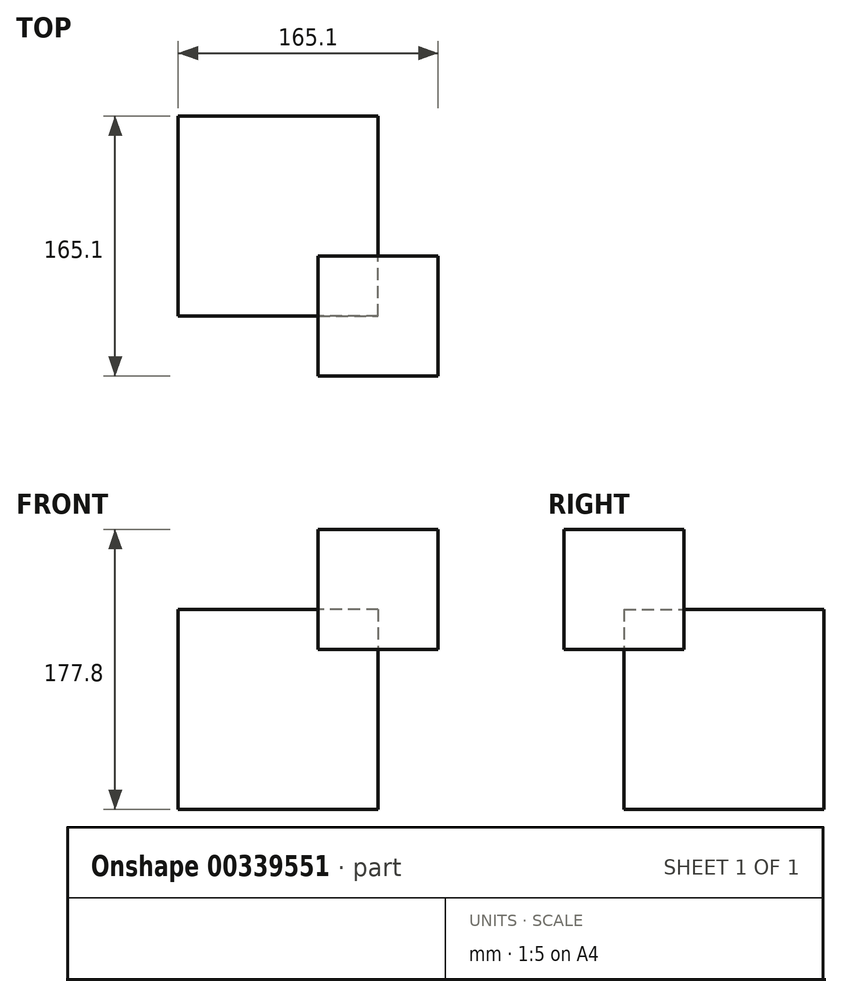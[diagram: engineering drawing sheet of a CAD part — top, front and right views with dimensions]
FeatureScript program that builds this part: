
annotation { "Feature Type Name" : "Feature", "Feature Type Description" : "" }
export const myFeature = defineFeature(function(context is Context, id is Id, definition is map)
    precondition{}
    {
        {
            var Q0;
            Q0=qCreatedBy(makeId("Front.planeOp"),FACE);
            var sketch = newSketch(context, id + "F0", { "sketchPlane" : qUnion([Q0])});
            skLineSegment(sketch, "E0.bottom", {"start": v(63.5, 63.5) * mm, "end": v(-63.5, 63.5) * mm});
            skLineSegment(sketch, "E0.top", {"start": v(63.5, -63.5) * mm, "end": v(-63.5, -63.5) * mm});
            skLineSegment(sketch, "E0.left", {"start": v(63.5, 63.5) * mm, "end": v(63.5, -63.5) * mm});
            skLineSegment(sketch, "E0.right", {"start": v(-63.5, 63.5) * mm, "end": v(-63.5, -63.5) * mm});
            skPoint(sketch, "E0.middle", {"position": v(0, 0) * mm});
            skSolve(sketch);
        }
        {
            var Q0;
            Q0=makeQuery(id+"F0.imprint","IMPRINT",FACE,{"disambiguationData":[TD([[makeQuery(id+"F0.imprint","IMPRINT",EDGE,{"derivedFrom":sQuery(id+"F0.wireOp",EDGE,"E0.bottom")}),1.0]])]});
            extrude(context, id + "F1", {"entities" : qUnion([Q0]), "endBound" : BoundingType.SYMMETRIC, "depth" : 127 * mm});
        }
        {
            var Q0;
            Q0=qCreatedBy(makeId("Top.planeOp"),FACE);
            cPlane(context, id + "F2", {"entities" : qUnion([Q0]), "cplaneType" : CPlaneType.OFFSET, "offset" : 38.1 * mm, "width" : 152.4 * mm, "height" : 152.4 * mm});
        }
        {
            var Q0;
            Q0=qCreatedBy(id+"F2.planeOp",FACE);
            var sketch = newSketch(context, id + "F3", { "sketchPlane" : qUnion([Q0])});
            skLineSegment(sketch, "E1.0.0", {"start": v(63.5, 63.5) * mm, "end": v(-63.5, 63.5) * mm});
            skLineSegment(sketch, "E1.0.1", {"start": v(-63.5, 63.5) * mm, "end": v(-63.5, -63.5) * mm});
            skLineSegment(sketch, "E1.0.2", {"start": v(-63.5, -63.5) * mm, "end": v(63.5, -63.5) * mm});
            skLineSegment(sketch, "E1.0.3", {"start": v(63.5, -63.5) * mm, "end": v(63.5, 63.5) * mm});
            skLineSegment(sketch, "E2.bottom", {"start": v(101.6, -25.4) * mm, "end": v(25.4, -25.4) * mm});
            skLineSegment(sketch, "E2.top", {"start": v(101.6, -101.6) * mm, "end": v(25.4, -101.6) * mm});
            skLineSegment(sketch, "E2.left", {"start": v(101.6, -25.4) * mm, "end": v(101.6, -101.6) * mm});
            skLineSegment(sketch, "E2.right", {"start": v(25.4, -25.4) * mm, "end": v(25.4, -101.6) * mm});
            skPoint(sketch, "E2.middle", {"position": v(63.5, -63.5) * mm});
            skSolve(sketch);
        }
        {
            var Q0;
            {var subQ6=sQuery(id+"F3.wireOp",EDGE,"E2.top");Q0=makeQuery(id+"F3.imprint","IMPRINT",FACE,{"disambiguationData":[TD([[makeQuery(id+"F3.imprint","IMPRINT",EDGE,{"derivedFrom":subQ6}),-1.0]])]});}
            extrude(context, id + "F4", {"entities" : qUnion([Q0]), "operationType" : NewBodyOperationType.ADD, "depth" : 76.2 * mm});
        }
        {
            var Q0;
            Q0=makeQuery(id+"F1.opExtrude","SWEPT_FACE",FACE,{"disambiguationData":[OSD([sQuery(id+"F0.wireOp",EDGE,"E0.bottom")])]});
            var sketch = newSketch(context, id + "F5", { "sketchPlane" : qUnion([Q0])});
            skLineSegment(sketch, "E3.0.0", {"start": v(101.6, -101.6) * mm, "end": v(101.6, -25.4) * mm});
            skLineSegment(sketch, "E3.0.1", {"start": v(101.6, -25.4) * mm, "end": v(63.5, -25.4) * mm});
            skLineSegment(sketch, "E3.0.2", {"start": v(63.5, -25.4) * mm, "end": v(63.5, -63.5) * mm});
            skLineSegment(sketch, "E3.0.3", {"start": v(63.5, -63.5) * mm, "end": v(25.4, -63.5) * mm});
            skLineSegment(sketch, "E3.0.4", {"start": v(25.4, -63.5) * mm, "end": v(25.4, -101.6) * mm});
            skLineSegment(sketch, "E3.0.5", {"start": v(25.4, -101.6) * mm, "end": v(101.6, -101.6) * mm});
            skLineSegment(sketch, "E4.0.0", {"start": v(63.5, 63.5) * mm, "end": v(-63.5, 63.5) * mm});
            skLineSegment(sketch, "E4.0.1", {"start": v(-63.5, 63.5) * mm, "end": v(-63.5, -63.5) * mm});
            skLineSegment(sketch, "E4.0.2", {"start": v(-63.5, -63.5) * mm, "end": v(25.4, -63.5) * mm});
            skLineSegment(sketch, "E4.0.3", {"start": v(25.4, -63.5) * mm, "end": v(63.5, -63.5) * mm});
            skLineSegment(sketch, "E4.0.4", {"start": v(63.5, -63.5) * mm, "end": v(63.5, -25.4) * mm});
            skLineSegment(sketch, "E4.0.5", {"start": v(63.5, -25.4) * mm, "end": v(63.5, 63.5) * mm});
            skLineSegment(sketch, "E5.top", {"start": v(63.5, -25.4) * mm, "end": v(25.4, -25.4) * mm});
            skLineSegment(sketch, "E5.right", {"start": v(25.4, -63.5) * mm, "end": v(25.4, -25.4) * mm});
            skSolve(sketch);
        }
        {
            var Q0;
            Q0=makeQuery(id+"F5.imprint","IMPRINT",FACE,{"disambiguationData":[TD([[makeQuery(id+"F5.imprint","IMPRINT",EDGE,{"derivedFrom":sQuery(id+"F5.wireOp",EDGE,"E3.0.3")}),-1.0]])]});
            extrude(context, id + "F6", {"entities" : qUnion([Q0]), "operationType" : NewBodyOperationType.ADD, "depth" : 50.8 * mm});
        }
    });
